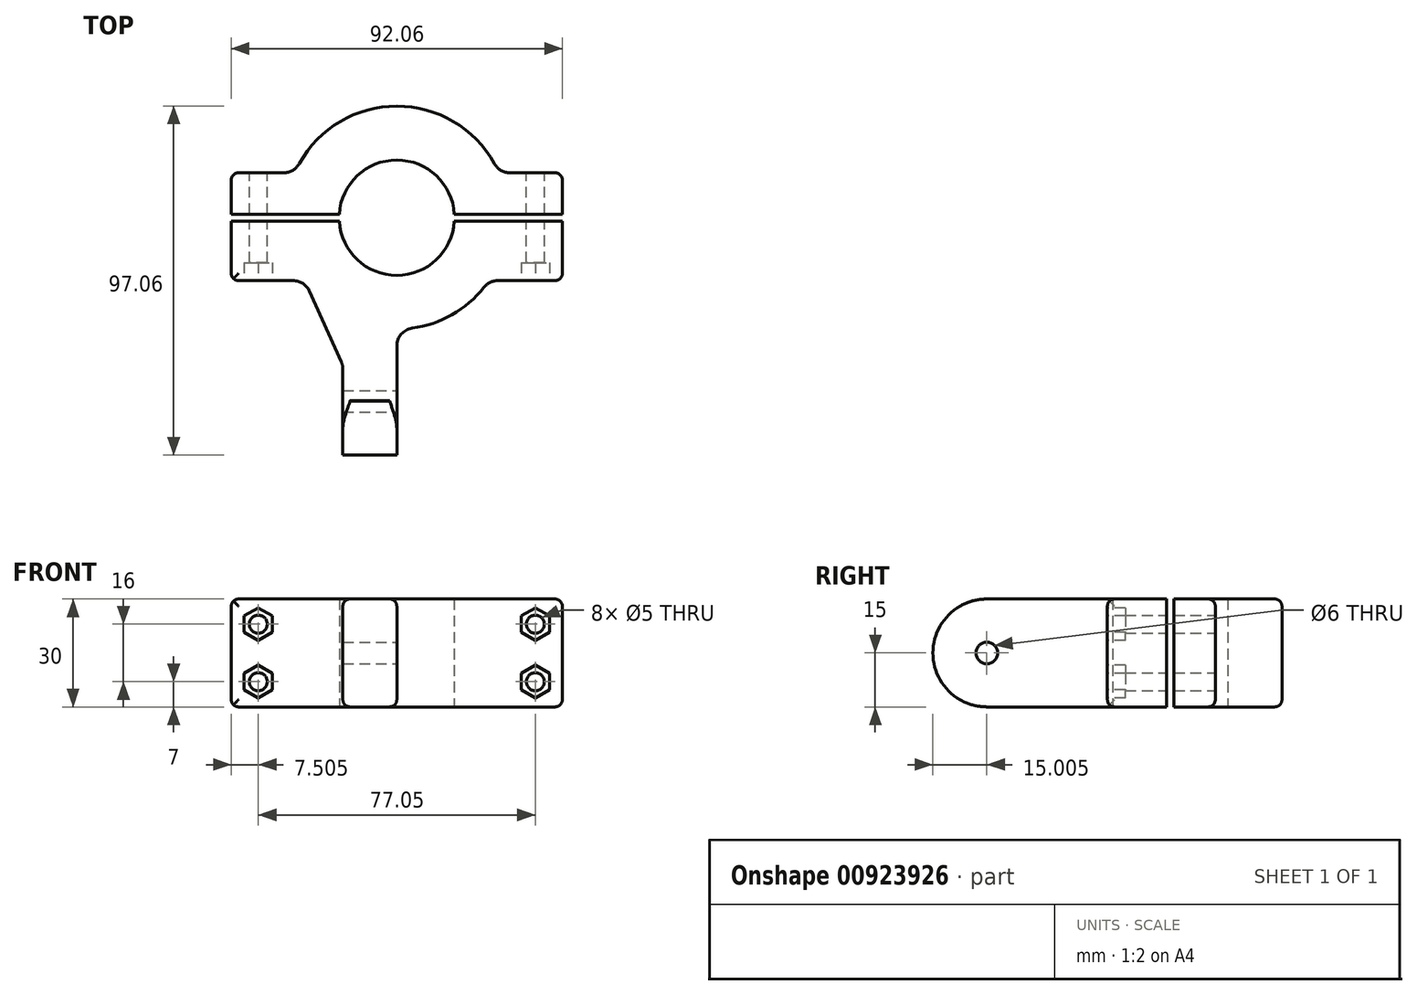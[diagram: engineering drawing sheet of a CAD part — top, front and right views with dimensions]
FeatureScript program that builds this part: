
annotation { "Feature Type Name" : "Feature", "Feature Type Description" : "" }
export const myFeature = defineFeature(function(context is Context, id is Id, definition is map)
    precondition{}
    {
        {
            var Q0;
            Q0=qCreatedBy(makeId("Top.planeOp"),FACE);
            var sketch = newSketch(context, id + "F0", { "sketchPlane" : qUnion([Q0])});
            skArc(sketch, "E0", {"start": v(-16, -1) * mm, "mid": v(0, -16.03) * mm, "end": v(16, -1) * mm});
            skLineSegment(sketch, "E1", {"start": v(-25.62, -17.5) * mm, "end": v(-25.62, -17.5) * mm});
            skLineSegment(sketch, "E2.bottom", {"start": v(-46.02, 12.5) * mm, "end": v(-28.4, 12.5) * mm});
            skLineSegment(sketch, "E2.top", {"start": v(-46.02, -17.5) * mm, "end": v(-25.62, -17.5) * mm});
            skLineSegment(sketch, "E2.left", {"start": v(-46.02, 12.5) * mm, "end": v(-46.02, 1) * mm});
            skLineSegment(sketch, "E2.right", {"start": v(46.02, 12.5) * mm, "end": v(46.02, 1) * mm});
            skLineSegment(sketch, "E3.trimOffspring", {"start": v(28.4, 12.5) * mm, "end": v(46.02, 12.5) * mm});
            skLineSegment(sketch, "E4.trimOffspring", {"start": v(25.62, -17.5) * mm, "end": v(46.02, -17.5) * mm});
            skArc(sketch, "E5.trimOffspring", {"start": v(28.4, 12.5) * mm, "mid": v(0, 31.02) * mm, "end": v(-28.4, 12.5) * mm});
            skLineSegment(sketch, "E6", {"start": v(-46.02, -1) * mm, "end": v(-16, -1) * mm});
            skLineSegment(sketch, "E7", {"start": v(46.02, 1) * mm, "end": v(16, 1) * mm});
            skLineSegment(sketch, "E8.trimOffspring", {"start": v(-46.02, -1) * mm, "end": v(-46.02, -17.5) * mm});
            skArc(sketch, "E9.trimOffspring", {"start": v(16, 1) * mm, "mid": v(0, 16.03) * mm, "end": v(-16, 1) * mm});
            skLineSegment(sketch, "E10.trimOffspring", {"start": v(46.02, -1) * mm, "end": v(46.02, -17.5) * mm});
            skLineSegment(sketch, "E11.trimOffspring", {"start": v(16, -1) * mm, "end": v(46.02, -1) * mm});
            skLineSegment(sketch, "E12.trimOffspring", {"start": v(-16, 1) * mm, "end": v(-46.02, 1) * mm});
            skLineSegment(sketch, "E13", {"start": v(0, -31.02) * mm, "end": v(0, -66.03) * mm});
            skLineSegment(sketch, "E14", {"start": v(0, -66.03) * mm, "end": v(-15, -66.03) * mm});
            skLineSegment(sketch, "E15", {"start": v(-15, -66.03) * mm, "end": v(-15, -41.03) * mm});
            skArc(sketch, "E16.trimOffspring", {"start": v(0, -31.02) * mm, "mid": v(14.48, -27.44) * mm, "end": v(25.62, -17.5) * mm});
            skLineSegment(sketch, "E17", {"start": v(-15, -41.03) * mm, "end": v(-25.62, -17.5) * mm});
            skSolve(sketch);
        }
        {
            var Q0;
            Q0 = qSketchRegion(id + "F0", true);
            extrude(context, id + "F1", {"entities" : qUnion([Q0]), "depth" : 30 * mm, "offsetDistance" : 25 * mm});
        }
        {
            var Q0;
            Q0=makeQuery(id+"F1.opExtrude","SWEPT_FACE",FACE,{"disambiguationData":[OSD([sQuery(id+"F0.wireOp",EDGE,"E3.trimOffspring")])]});
            var sketch = newSketch(context, id + "F2", { "sketchPlane" : qUnion([Q0])});
            skPoint(sketch, "E18", {"position": v(-38.52, 23) * mm});
            skPoint(sketch, "E19", {"position": v(-38.52, 7) * mm});
            skPoint(sketch, "E20", {"position": v(38.52, 23) * mm});
            skPoint(sketch, "E21", {"position": v(38.52, 7) * mm});
            skSolve(sketch);
        }
        {
            var Q0;
            Q0=sQuery(id+"F2.wireOp",VERTEX,"E20");
            var Q1;
            Q1=sQuery(id+"F2.wireOp",VERTEX,"E21");
            var Q2;
            Q2=sQuery(id+"F2.wireOp",VERTEX,"E18");
            var Q3;
            Q3=sQuery(id+"F2.wireOp",VERTEX,"E19");
            var Q4;
            Q4=makeQuery(id+"F1.opExtrude","SWEPT_BODY",BODY,{"disambiguationData":[OSD([sQuery(id+"F0.wireOp",EDGE,"E0"),sQuery(id+"F0.wireOp",EDGE,"E1"),sQuery(id+"F0.wireOp",EDGE,"E2.top"),sQuery(id+"F0.wireOp",EDGE,"E4.trimOffspring"),sQuery(id+"F0.wireOp",EDGE,"E6"),sQuery(id+"F0.wireOp",EDGE,"E8.trimOffspring"),sQuery(id+"F0.wireOp",EDGE,"E10.trimOffspring"),sQuery(id+"F0.wireOp",EDGE,"E11.trimOffspring"),sQuery(id+"F0.wireOp",EDGE,"E13"),sQuery(id+"F0.wireOp",EDGE,"E14"),sQuery(id+"F0.wireOp",EDGE,"E15"),sQuery(id+"F0.wireOp",EDGE,"E16.trimOffspring"),sQuery(id+"F0.wireOp",EDGE,"E17")])]});
            var Q5;
            Q5=makeQuery(id+"F1.opExtrude","SWEPT_BODY",BODY,{"disambiguationData":[OSD([sQuery(id+"F0.wireOp",EDGE,"E2.bottom"),sQuery(id+"F0.wireOp",EDGE,"E2.left"),sQuery(id+"F0.wireOp",EDGE,"E2.right"),sQuery(id+"F0.wireOp",EDGE,"E3.trimOffspring"),sQuery(id+"F0.wireOp",EDGE,"E5.trimOffspring"),sQuery(id+"F0.wireOp",EDGE,"E7"),sQuery(id+"F0.wireOp",EDGE,"E9.trimOffspring"),sQuery(id+"F0.wireOp",EDGE,"E12.trimOffspring")])]});
            hole(context, id + "F3", {"style" : HoleStyle.SIMPLE, "endStyle" : HoleEndStyle.BLIND, "holeDiameter" : 5 * mm, "majorDiameter" : 5 * mm, "holeDepth" : 35 * mm, "isTappedThrough" : true, "tappedDepth" : 12 * mm, "tapClearance" : 3, "startFromSketch" : true, "locations" : qUnion([Q0, Q1, Q2, Q3]), "scope" : qUnion([Q4, Q5])});
        }
        {
            var Q0;
            Q0=makeQuery(id+"F1.opExtrude","SWEPT_EDGE",EDGE,{"disambiguationData":[OSD([sQuery(id+"F0.wireOp",EDGE,"E2.bottom"),sQuery(id+"F0.wireOp",EDGE,"E5.trimOffspring")])]});
            var Q1;
            Q1=makeQuery(id+"F1.opExtrude","SWEPT_EDGE",EDGE,{"disambiguationData":[OSD([sQuery(id+"F0.wireOp",EDGE,"E3.trimOffspring"),sQuery(id+"F0.wireOp",EDGE,"E5.trimOffspring")])]});
            var Q2;
            Q2=makeQuery(id+"F1.opExtrude","SWEPT_EDGE",EDGE,{"disambiguationData":[OSD([sQuery(id+"F0.wireOp",EDGE,"E4.trimOffspring"),sQuery(id+"F0.wireOp",EDGE,"E16.trimOffspring")])]});
            var Q3;
            Q3=makeQuery(id+"F1.opExtrude","SWEPT_EDGE",EDGE,{"disambiguationData":[OSD([sQuery(id+"F0.wireOp",EDGE,"E1"),sQuery(id+"F0.wireOp",EDGE,"E2.top"),sQuery(id+"F0.wireOp",EDGE,"E17")])]});
            var Q4;
            Q4=makeQuery(id+"F1.opExtrude","SWEPT_EDGE",EDGE,{"disambiguationData":[OSD([sQuery(id+"F0.wireOp",EDGE,"E15"),sQuery(id+"F0.wireOp",EDGE,"E17")])]});
            var Q5;
            Q5=makeQuery(id+"F1.opExtrude","SWEPT_EDGE",EDGE,{"disambiguationData":[OSD([sQuery(id+"F0.wireOp",EDGE,"E13"),sQuery(id+"F0.wireOp",EDGE,"E16.trimOffspring")])]});
            fillet(context, id + "F4", {"entities" : qUnion([Q0, Q1, Q2, Q3, Q4, Q5]), "radius" : 5 * mm, "tangentPropagation" : true, "allowEdgeOverflow" : false});
        }
        {
            var Q0;
            Q0=makeQuery(id+"F1.opExtrude","SWEPT_FACE",FACE,{"disambiguationData":[OSD([sQuery(id+"F0.wireOp",EDGE,"E2.top")])]});
            var sketch = newSketch(context, id + "F5", { "sketchPlane" : qUnion([Q0])});
            skCircle(sketch, "E22.cCircle", {"center": v(-38.52, 23) * mm, "radius": 3.95 * mm, "construction": true});
            skLineSegment(sketch, "E22.0", {"start": v(-34.57, 25.28) * mm, "end": v(-34.57, 20.72) * mm});
            skLineSegment(sketch, "E22.1", {"start": v(-34.57, 20.72) * mm, "end": v(-38.52, 18.44) * mm});
            skLineSegment(sketch, "E22.2", {"start": v(-38.52, 18.44) * mm, "end": v(-42.48, 20.72) * mm});
            skLineSegment(sketch, "E22.3", {"start": v(-42.48, 20.72) * mm, "end": v(-42.48, 25.28) * mm});
            skLineSegment(sketch, "E22.4", {"start": v(-42.48, 25.28) * mm, "end": v(-38.53, 27.56) * mm});
            skLineSegment(sketch, "E22.5", {"start": v(-38.52, 27.56) * mm, "end": v(-34.57, 25.28) * mm});
            skPoint(sketch, "E22.0.midPoint", {"position": v(-34.57, 23) * mm});
            skCircle(sketch, "E23.cCircle", {"center": v(-38.52, 7) * mm, "radius": 3.95 * mm, "construction": true});
            skLineSegment(sketch, "E23.0", {"start": v(-34.57, 9.28) * mm, "end": v(-34.57, 4.72) * mm});
            skLineSegment(sketch, "E23.1", {"start": v(-34.57, 4.72) * mm, "end": v(-38.52, 2.44) * mm});
            skLineSegment(sketch, "E23.2", {"start": v(-38.52, 2.44) * mm, "end": v(-42.48, 4.72) * mm});
            skLineSegment(sketch, "E23.3", {"start": v(-42.48, 4.72) * mm, "end": v(-42.48, 9.28) * mm});
            skLineSegment(sketch, "E23.4", {"start": v(-42.48, 9.28) * mm, "end": v(-38.53, 11.56) * mm});
            skLineSegment(sketch, "E23.5", {"start": v(-38.52, 11.56) * mm, "end": v(-34.57, 9.28) * mm});
            skPoint(sketch, "E23.0.midPoint", {"position": v(-34.57, 7) * mm});
            skSolve(sketch);
        }
        {
            var Q0;
            Q0=makeQuery(id+"F1.opExtrude","SWEPT_FACE",FACE,{"disambiguationData":[OSD([sQuery(id+"F0.wireOp",EDGE,"E4.trimOffspring")])]});
            var sketch = newSketch(context, id + "F6", { "sketchPlane" : qUnion([Q0])});
            skCircle(sketch, "E24.cCircle", {"center": v(38.52, 23) * mm, "radius": 3.95 * mm, "construction": true});
            skLineSegment(sketch, "E24.0", {"start": v(38.53, 27.56) * mm, "end": v(42.48, 25.28) * mm});
            skLineSegment(sketch, "E24.1", {"start": v(42.48, 25.28) * mm, "end": v(42.48, 20.72) * mm});
            skLineSegment(sketch, "E24.2", {"start": v(42.47, 20.72) * mm, "end": v(38.52, 18.44) * mm});
            skLineSegment(sketch, "E24.3", {"start": v(38.52, 18.44) * mm, "end": v(34.58, 20.72) * mm});
            skLineSegment(sketch, "E24.4", {"start": v(34.58, 20.72) * mm, "end": v(34.58, 25.28) * mm});
            skLineSegment(sketch, "E24.5", {"start": v(34.58, 25.28) * mm, "end": v(38.53, 27.56) * mm});
            skPoint(sketch, "E24.0.midPoint", {"position": v(40.5, 26.42) * mm});
            skCircle(sketch, "E25.cCircle", {"center": v(38.52, 7) * mm, "radius": 3.95 * mm, "construction": true});
            skLineSegment(sketch, "E25.0", {"start": v(38.52, 11.56) * mm, "end": v(42.48, 9.28) * mm});
            skLineSegment(sketch, "E25.1", {"start": v(42.47, 9.28) * mm, "end": v(42.47, 4.72) * mm});
            skLineSegment(sketch, "E25.2", {"start": v(42.47, 4.72) * mm, "end": v(38.52, 2.44) * mm});
            skLineSegment(sketch, "E25.3", {"start": v(38.53, 2.44) * mm, "end": v(34.58, 4.72) * mm});
            skLineSegment(sketch, "E25.4", {"start": v(34.57, 4.72) * mm, "end": v(34.57, 9.28) * mm});
            skLineSegment(sketch, "E25.5", {"start": v(34.57, 9.28) * mm, "end": v(38.52, 11.56) * mm});
            skPoint(sketch, "E25.0.midPoint", {"position": v(40.5, 10.42) * mm});
            skSolve(sketch);
        }
        {
            var Q0;
            Q0=makeQuery(id+"F5.imprint","IMPRINT",FACE,{"disambiguationData":[TD([[makeQuery(id+"F5.imprint","IMPRINT",EDGE,{"derivedFrom":sQuery(id+"F5.wireOp",EDGE,"E22.0")}),-1.0]])]});
            var Q1;
            Q1=makeQuery(id+"F5.imprint","IMPRINT",FACE,{"disambiguationData":[TD([[makeQuery(id+"F5.imprint","IMPRINT",EDGE,{"derivedFrom":sQuery(id+"F5.wireOp",EDGE,"E23.0")}),-1.0]])]});
            var Q2;
            Q2=makeQuery(id+"F6.imprint","IMPRINT",FACE,{"disambiguationData":[TD([[makeQuery(id+"F6.imprint","IMPRINT",EDGE,{"derivedFrom":sQuery(id+"F6.wireOp",EDGE,"E24.0")}),-1.0]])]});
            var Q3;
            Q3=makeQuery(id+"F6.imprint","IMPRINT",FACE,{"disambiguationData":[TD([[makeQuery(id+"F6.imprint","IMPRINT",EDGE,{"derivedFrom":sQuery(id+"F6.wireOp",EDGE,"E25.0")}),-1.0]])]});
            extrude(context, id + "F7", {"entities" : qUnion([Q0, Q1, Q2, Q3]), "operationType" : NewBodyOperationType.REMOVE, "oppositeDirection" : true, "depth" : 5 * mm, "offsetDistance" : 25 * mm});
        }
        {
            var Q0;
            Q0=makeQuery(id+"F1.opExtrude","CAP_EDGE",EDGE,{"disambiguationData":[OSD([sQuery(id+"F0.wireOp",EDGE,"E5.trimOffspring")])],"isStart":false});
            var Q1;
            Q1=makeQuery(id+"F1.opExtrude","SWEPT_EDGE",EDGE,{"disambiguationData":[OSD([sQuery(id+"F0.wireOp",EDGE,"E2.bottom"),sQuery(id+"F0.wireOp",EDGE,"E2.left")])]});
            var Q2;
            Q2=makeQuery(id+"F1.opExtrude","CAP_EDGE",EDGE,{"disambiguationData":[OSD([sQuery(id+"F0.wireOp",EDGE,"E5.trimOffspring")])],"isStart":true});
            var Q3;
            Q3=makeQuery(id+"F1.opExtrude","SWEPT_EDGE",EDGE,{"disambiguationData":[OSD([sQuery(id+"F0.wireOp",EDGE,"E2.right"),sQuery(id+"F0.wireOp",EDGE,"E3.trimOffspring")])]});
            var Q4;
            Q4=makeQuery(id+"F1.opExtrude","CAP_EDGE",EDGE,{"disambiguationData":[OSD([sQuery(id+"F0.wireOp",EDGE,"E2.left")])],"isStart":false});
            var Q5;
            Q5=makeQuery(id+"F1.opExtrude","CAP_EDGE",EDGE,{"disambiguationData":[OSD([sQuery(id+"F0.wireOp",EDGE,"E2.left")])],"isStart":true});
            var Q6;
            Q6=makeQuery(id+"F1.opExtrude","CAP_EDGE",EDGE,{"disambiguationData":[OSD([sQuery(id+"F0.wireOp",EDGE,"E8.trimOffspring")])],"isStart":true});
            var Q7;
            Q7=makeQuery(id+"F1.opExtrude","CAP_EDGE",EDGE,{"disambiguationData":[OSD([sQuery(id+"F0.wireOp",EDGE,"E8.trimOffspring")])],"isStart":false});
            var Q8;
            Q8=makeQuery(id+"F1.opExtrude","CAP_EDGE",EDGE,{"disambiguationData":[OSD([sQuery(id+"F0.wireOp",EDGE,"E10.trimOffspring")])],"isStart":false});
            var Q9;
            Q9=makeQuery(id+"F1.opExtrude","CAP_EDGE",EDGE,{"disambiguationData":[OSD([sQuery(id+"F0.wireOp",EDGE,"E10.trimOffspring")])],"isStart":true});
            var Q10;
            Q10=makeQuery(id+"F1.opExtrude","SWEPT_EDGE",EDGE,{"disambiguationData":[OSD([sQuery(id+"F0.wireOp",EDGE,"E4.trimOffspring"),sQuery(id+"F0.wireOp",EDGE,"E10.trimOffspring")])]});
            var Q11;
            Q11=makeQuery(id+"F1.opExtrude","CAP_EDGE",EDGE,{"disambiguationData":[OSD([sQuery(id+"F0.wireOp",EDGE,"E4.trimOffspring")])],"isStart":true});
            var Q12;
            Q12=makeQuery(id+"F1.opExtrude","CAP_EDGE",EDGE,{"disambiguationData":[OSD([sQuery(id+"F0.wireOp",EDGE,"E4.trimOffspring")])],"isStart":false});
            var Q13;
            Q13=makeQuery(id+"F1.opExtrude","SWEPT_EDGE",EDGE,{"disambiguationData":[OSD([sQuery(id+"F0.wireOp",EDGE,"E2.top"),sQuery(id+"F0.wireOp",EDGE,"E8.trimOffspring")])]});
            fillet(context, id + "F8", {"entities" : qUnion([Q0, Q1, Q2, Q3, Q4, Q5, Q6, Q7, Q8, Q9, Q10, Q11, Q12, Q13]), "radius" : 2 * mm, "tangentPropagation" : true, "allowEdgeOverflow" : false});
        }
        {
            var Q0;
            Q0=makeQuery(id+"F1.opExtrude","CAP_EDGE",EDGE,{"disambiguationData":[OSD([sQuery(id+"F0.wireOp",EDGE,"E2.right")])],"isStart":false});
            var Q1;
            Q1=makeQuery(id+"F1.opExtrude","CAP_EDGE",EDGE,{"disambiguationData":[OSD([sQuery(id+"F0.wireOp",EDGE,"E2.right")])],"isStart":true});
            fillet(context, id + "F9", {"entities" : qUnion([Q0, Q1]), "radius" : 2 * mm, "tangentPropagation" : true, "allowEdgeOverflow" : false});
        }
        {
            var Q0;
            Q0=makeQuery(id+"F1.opExtrude","SWEPT_FACE",FACE,{"disambiguationData":[OSD([sQuery(id+"F0.wireOp",EDGE,"E13")])]});
            var sketch = newSketch(context, id + "F10", { "sketchPlane" : qUnion([Q0])});
            skPoint(sketch, "E26", {"position": v(-51.02, 15) * mm});
            skArc(sketch, "E27", {"start": v(-50.85, 30) * mm, "mid": v(-66.02, 15.09) * mm, "end": v(-51.02, 0) * mm});
            skLineSegment(sketch, "E28", {"start": v(-50.85, 30) * mm, "end": v(-66.03, 30.18) * mm});
            skPoint(sketch, "E28.startSnap0", {"position": v(-50.85, 28) * mm});
            skLineSegment(sketch, "E29", {"start": v(-66.03, 30.18) * mm, "end": v(-66.03, 0) * mm});
            skLineSegment(sketch, "E30", {"start": v(-66.03, 0) * mm, "end": v(-51.02, 0) * mm});
            skSolve(sketch);
        }
        {
            var Q0;
            Q0=sQuery(id+"F10.wireOp",VERTEX,"E26");
            var Q1;
            Q1=makeQuery(id+"F1.opExtrude","SWEPT_BODY",BODY,{"disambiguationData":[OSD([sQuery(id+"F0.wireOp",EDGE,"E0"),sQuery(id+"F0.wireOp",EDGE,"E2.top"),sQuery(id+"F0.wireOp",EDGE,"E4.trimOffspring"),sQuery(id+"F0.wireOp",EDGE,"E6"),sQuery(id+"F0.wireOp",EDGE,"E8.trimOffspring"),sQuery(id+"F0.wireOp",EDGE,"E10.trimOffspring"),sQuery(id+"F0.wireOp",EDGE,"E11.trimOffspring"),sQuery(id+"F0.wireOp",EDGE,"E13"),sQuery(id+"F0.wireOp",EDGE,"E14"),sQuery(id+"F0.wireOp",EDGE,"E15"),sQuery(id+"F0.wireOp",EDGE,"E16.trimOffspring"),sQuery(id+"F0.wireOp",EDGE,"E17")])]});
            hole(context, id + "F11", {"style" : HoleStyle.SIMPLE, "endStyle" : HoleEndStyle.BLIND, "holeDiameter" : 6 * mm, "majorDiameter" : 5 * mm, "holeDepth" : 35 * mm, "isTappedThrough" : true, "tappedDepth" : 12 * mm, "tapClearance" : 3, "startFromSketch" : true, "locations" : qUnion([Q0]), "scope" : qUnion([Q1])});
        }
        {
            var Q0;
            Q0 = qSketchRegion(id + "F10", true);
            extrude(context, id + "F12", {"entities" : qUnion([Q0]), "operationType" : NewBodyOperationType.REMOVE, "oppositeDirection" : true, "depth" : 25 * mm, "offsetDistance" : 25 * mm});
        }
        {
            var Q0;
            Q0=makeQuery(id+"F1.opExtrude","CAP_EDGE",EDGE,{"disambiguationData":[OSD([sQuery(id+"F0.wireOp",EDGE,"E2.top")])],"isStart":false});
            var Q1;
            Q1=makeQuery(id+"F1.opExtrude","CAP_EDGE",EDGE,{"disambiguationData":[OSD([sQuery(id+"F0.wireOp",EDGE,"E2.top")])],"isStart":true});
            var Q2;
            Q2=makeQuery(id+"F1.opExtrude","CAP_EDGE",EDGE,{"disambiguationData":[OSD([sQuery(id+"F0.wireOp",EDGE,"E17")])],"isStart":true});
            var Q3;
            {var subQ0=sQuery(id+"F0.wireOp",EDGE,"E17");var subQ1=sQuery(id+"F0.wireOp",EDGE,"E2.top");Q3=makeQuery(id+"F4.opFillet","BLEND_EDGE",EDGE,{"blendedFrom":[makeQuery(id+"F1.opExtrude","SWEPT_EDGE",EDGE,{"disambiguationData":[OSD([subQ1,subQ0])]}),makeQuery(id+"F1.opExtrude","CAP_FACE",FACE,{"disambiguationData":[OSD([sQuery(id+"F0.wireOp",EDGE,"E0"),subQ1,sQuery(id+"F0.wireOp",EDGE,"E4.trimOffspring"),sQuery(id+"F0.wireOp",EDGE,"E6"),sQuery(id+"F0.wireOp",EDGE,"E8.trimOffspring"),sQuery(id+"F0.wireOp",EDGE,"E10.trimOffspring"),sQuery(id+"F0.wireOp",EDGE,"E11.trimOffspring"),sQuery(id+"F0.wireOp",EDGE,"E13"),sQuery(id+"F0.wireOp",EDGE,"E14"),sQuery(id+"F0.wireOp",EDGE,"E15"),sQuery(id+"F0.wireOp",EDGE,"E16.trimOffspring"),subQ0])],"isStart":true})],"blendedInto":[makeQuery(id+"F1.opExtrude","CAP_FACE",FACE,{"disambiguationData":[OSD([sQuery(id+"F0.wireOp",EDGE,"E0"),subQ1,sQuery(id+"F0.wireOp",EDGE,"E4.trimOffspring"),sQuery(id+"F0.wireOp",EDGE,"E6"),sQuery(id+"F0.wireOp",EDGE,"E8.trimOffspring"),sQuery(id+"F0.wireOp",EDGE,"E10.trimOffspring"),sQuery(id+"F0.wireOp",EDGE,"E11.trimOffspring"),sQuery(id+"F0.wireOp",EDGE,"E13"),sQuery(id+"F0.wireOp",EDGE,"E14"),sQuery(id+"F0.wireOp",EDGE,"E15"),sQuery(id+"F0.wireOp",EDGE,"E16.trimOffspring"),subQ0])],"isStart":true})]});}
            var Q4;
            {var subQ0=sQuery(id+"F0.wireOp",EDGE,"E17");var subQ1=sQuery(id+"F0.wireOp",EDGE,"E2.top");Q4=makeQuery(id+"F4.opFillet","BLEND_EDGE",EDGE,{"blendedFrom":[makeQuery(id+"F1.opExtrude","SWEPT_EDGE",EDGE,{"disambiguationData":[OSD([subQ1,subQ0])]}),makeQuery(id+"F1.opExtrude","CAP_FACE",FACE,{"disambiguationData":[OSD([sQuery(id+"F0.wireOp",EDGE,"E0"),subQ1,sQuery(id+"F0.wireOp",EDGE,"E4.trimOffspring"),sQuery(id+"F0.wireOp",EDGE,"E6"),sQuery(id+"F0.wireOp",EDGE,"E8.trimOffspring"),sQuery(id+"F0.wireOp",EDGE,"E10.trimOffspring"),sQuery(id+"F0.wireOp",EDGE,"E11.trimOffspring"),sQuery(id+"F0.wireOp",EDGE,"E13"),sQuery(id+"F0.wireOp",EDGE,"E14"),sQuery(id+"F0.wireOp",EDGE,"E15"),sQuery(id+"F0.wireOp",EDGE,"E16.trimOffspring"),subQ0])],"isStart":false})],"blendedInto":[makeQuery(id+"F1.opExtrude","CAP_FACE",FACE,{"disambiguationData":[OSD([sQuery(id+"F0.wireOp",EDGE,"E0"),subQ1,sQuery(id+"F0.wireOp",EDGE,"E4.trimOffspring"),sQuery(id+"F0.wireOp",EDGE,"E6"),sQuery(id+"F0.wireOp",EDGE,"E8.trimOffspring"),sQuery(id+"F0.wireOp",EDGE,"E10.trimOffspring"),sQuery(id+"F0.wireOp",EDGE,"E11.trimOffspring"),sQuery(id+"F0.wireOp",EDGE,"E13"),sQuery(id+"F0.wireOp",EDGE,"E14"),sQuery(id+"F0.wireOp",EDGE,"E15"),sQuery(id+"F0.wireOp",EDGE,"E16.trimOffspring"),subQ0])],"isStart":false})]});}
            var Q5;
            Q5=makeQuery(id+"F1.opExtrude","CAP_EDGE",EDGE,{"disambiguationData":[OSD([sQuery(id+"F0.wireOp",EDGE,"E17")])],"isStart":false});
            var Q6;
            Q6=makeQuery(id+"F1.opExtrude","CAP_EDGE",EDGE,{"disambiguationData":[OSD([sQuery(id+"F0.wireOp",EDGE,"E15")])],"isStart":true});
            var Q7;
            {var subQ0=sQuery(id+"F0.wireOp",EDGE,"E17");var subQ1=sQuery(id+"F0.wireOp",EDGE,"E15");Q7=makeQuery(id+"F4.opFillet","BLEND_EDGE",EDGE,{"blendedFrom":[makeQuery(id+"F1.opExtrude","SWEPT_EDGE",EDGE,{"disambiguationData":[OSD([subQ1,subQ0])]}),makeQuery(id+"F1.opExtrude","CAP_FACE",FACE,{"disambiguationData":[OSD([sQuery(id+"F0.wireOp",EDGE,"E0"),sQuery(id+"F0.wireOp",EDGE,"E2.top"),sQuery(id+"F0.wireOp",EDGE,"E4.trimOffspring"),sQuery(id+"F0.wireOp",EDGE,"E6"),sQuery(id+"F0.wireOp",EDGE,"E8.trimOffspring"),sQuery(id+"F0.wireOp",EDGE,"E10.trimOffspring"),sQuery(id+"F0.wireOp",EDGE,"E11.trimOffspring"),sQuery(id+"F0.wireOp",EDGE,"E13"),sQuery(id+"F0.wireOp",EDGE,"E14"),subQ1,sQuery(id+"F0.wireOp",EDGE,"E16.trimOffspring"),subQ0])],"isStart":true})],"blendedInto":[makeQuery(id+"F1.opExtrude","CAP_FACE",FACE,{"disambiguationData":[OSD([sQuery(id+"F0.wireOp",EDGE,"E0"),sQuery(id+"F0.wireOp",EDGE,"E2.top"),sQuery(id+"F0.wireOp",EDGE,"E4.trimOffspring"),sQuery(id+"F0.wireOp",EDGE,"E6"),sQuery(id+"F0.wireOp",EDGE,"E8.trimOffspring"),sQuery(id+"F0.wireOp",EDGE,"E10.trimOffspring"),sQuery(id+"F0.wireOp",EDGE,"E11.trimOffspring"),sQuery(id+"F0.wireOp",EDGE,"E13"),sQuery(id+"F0.wireOp",EDGE,"E14"),subQ1,sQuery(id+"F0.wireOp",EDGE,"E16.trimOffspring"),subQ0])],"isStart":true})]});}
            var Q8;
            {var subQ0=sQuery(id+"F0.wireOp",EDGE,"E17");var subQ1=sQuery(id+"F0.wireOp",EDGE,"E15");Q8=makeQuery(id+"F4.opFillet","BLEND_EDGE",EDGE,{"blendedFrom":[makeQuery(id+"F1.opExtrude","SWEPT_EDGE",EDGE,{"disambiguationData":[OSD([subQ1,subQ0])]}),makeQuery(id+"F1.opExtrude","CAP_FACE",FACE,{"disambiguationData":[OSD([sQuery(id+"F0.wireOp",EDGE,"E0"),sQuery(id+"F0.wireOp",EDGE,"E2.top"),sQuery(id+"F0.wireOp",EDGE,"E4.trimOffspring"),sQuery(id+"F0.wireOp",EDGE,"E6"),sQuery(id+"F0.wireOp",EDGE,"E8.trimOffspring"),sQuery(id+"F0.wireOp",EDGE,"E10.trimOffspring"),sQuery(id+"F0.wireOp",EDGE,"E11.trimOffspring"),sQuery(id+"F0.wireOp",EDGE,"E13"),sQuery(id+"F0.wireOp",EDGE,"E14"),subQ1,sQuery(id+"F0.wireOp",EDGE,"E16.trimOffspring"),subQ0])],"isStart":false})],"blendedInto":[makeQuery(id+"F1.opExtrude","CAP_FACE",FACE,{"disambiguationData":[OSD([sQuery(id+"F0.wireOp",EDGE,"E0"),sQuery(id+"F0.wireOp",EDGE,"E2.top"),sQuery(id+"F0.wireOp",EDGE,"E4.trimOffspring"),sQuery(id+"F0.wireOp",EDGE,"E6"),sQuery(id+"F0.wireOp",EDGE,"E8.trimOffspring"),sQuery(id+"F0.wireOp",EDGE,"E10.trimOffspring"),sQuery(id+"F0.wireOp",EDGE,"E11.trimOffspring"),sQuery(id+"F0.wireOp",EDGE,"E13"),sQuery(id+"F0.wireOp",EDGE,"E14"),subQ1,sQuery(id+"F0.wireOp",EDGE,"E16.trimOffspring"),subQ0])],"isStart":false})]});}
            var Q9;
            Q9=makeQuery(id+"F1.opExtrude","CAP_EDGE",EDGE,{"disambiguationData":[OSD([sQuery(id+"F0.wireOp",EDGE,"E15")])],"isStart":false});
            fillet(context, id + "F13", {"entities" : qUnion([Q0, Q1, Q2, Q3, Q4, Q5, Q6, Q7, Q8, Q9]), "radius" : 2 * mm, "allowEdgeOverflow" : false});
        }
    });
